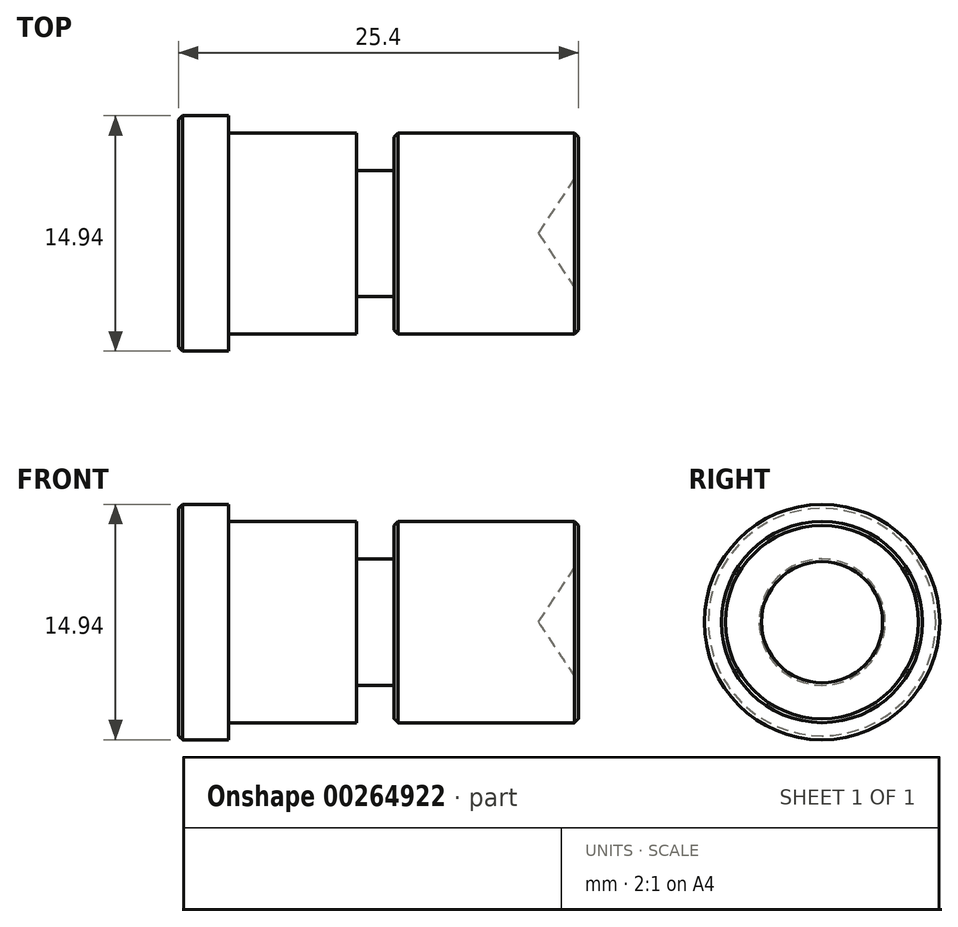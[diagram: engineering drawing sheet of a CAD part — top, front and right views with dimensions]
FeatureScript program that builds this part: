
annotation { "Feature Type Name" : "Feature", "Feature Type Description" : "" }
export const myFeature = defineFeature(function(context is Context, id is Id, definition is map)
    precondition{}
    {
        {
            var Q0;
            Q0=qCreatedBy(makeId("Front.planeOp"),FACE);
            var sketch = newSketch(context, id + "F0", { "sketchPlane" : qUnion([Q0])});
            skLineSegment(sketch, "E0.bottom", {"start": v(3.18, 6.39) * mm, "end": v(11.3, 6.39) * mm});
            skLineSegment(sketch, "E0.top", {"start": v(0, 0) * mm, "end": v(22.86, 0) * mm});
            skLineSegment(sketch, "E0.right", {"start": v(25.4, 6.39) * mm, "end": v(25.4, 3.85) * mm});
            skLineSegment(sketch, "E1.bottom", {"start": v(0, 7.47) * mm, "end": v(3.18, 7.47) * mm});
            skLineSegment(sketch, "E1.right", {"start": v(3.18, 7.47) * mm, "end": v(3.18, 6.39) * mm});
            skLineSegment(sketch, "E2.top", {"start": v(11.3, 4) * mm, "end": v(13.68, 4) * mm});
            skLineSegment(sketch, "E2.left", {"start": v(11.3, 6.39) * mm, "end": v(11.3, 4) * mm});
            skLineSegment(sketch, "E2.right", {"start": v(13.68, 6.39) * mm, "end": v(13.68, 4) * mm});
            skLineSegment(sketch, "E3.trimOffspring", {"start": v(13.68, 6.39) * mm, "end": v(25.4, 6.39) * mm});
            skLineSegment(sketch, "E4", {"start": v(25.4, 3.85) * mm, "end": v(25.4, 6.39) * mm});
            skLineSegment(sketch, "E5", {"start": v(22.86, 0) * mm, "end": v(25.4, 3.85) * mm});
            skLineSegment(sketch, "E6", {"start": v(0, 7.47) * mm, "end": v(0, 0) * mm});
            skPoint(sketch, "E7.orphan", {"position": v(25.4, 0) * mm});
            skSolve(sketch);
        }
        {
            var Q0;
            Q0=makeQuery(id+"F0.imprint","IMPRINT",FACE,{"disambiguationData":[TD([[makeQuery(id+"F0.imprint","IMPRINT",EDGE,{"derivedFrom":sQuery(id+"F0.wireOp",EDGE,"E0.bottom")}),-1.0]])]});
            var Q1;
            Q1=sQuery(id+"F0.wireOp",EDGE,"E0.top");
            revolve(context, id + "F1", {"entities" : qUnion([Q0]), "axis" : qUnion([Q1]), "revolveType" : RevolveType.FULL});
        }
        {
            var Q0;
            Q0=makeQuery(id+"F1.opRevolve","SWEPT_EDGE",EDGE,{"disambiguationData":[OSD([sQuery(id+"F0.wireOp",EDGE,"E1.bottom"),sQuery(id+"F0.wireOp",EDGE,"E6")])]});
            var Q1;
            Q1=makeQuery(id+"F1.opRevolve","SWEPT_EDGE",EDGE,{"disambiguationData":[OSD([sQuery(id+"F0.wireOp",EDGE,"E3.trimOffspring"),sQuery(id+"F0.wireOp",EDGE,"E4")])]});
            chamfer(context, id + "F2", {"entities" : qUnion([Q0, Q1]), "width" : 0.25 * mm, "tangentPropagation" : true});
        }
    });
